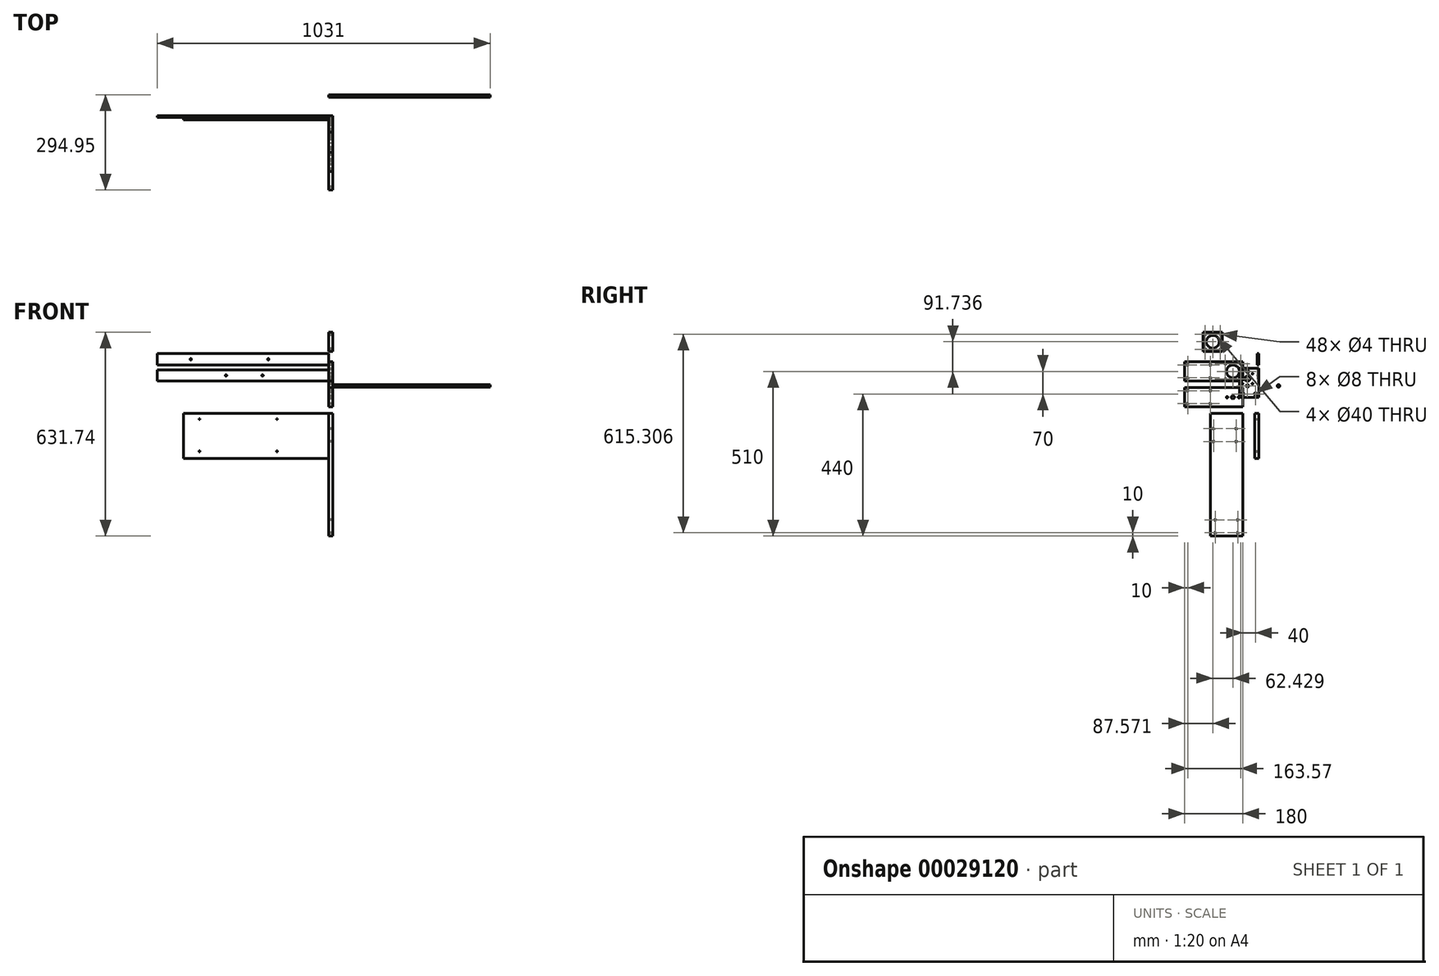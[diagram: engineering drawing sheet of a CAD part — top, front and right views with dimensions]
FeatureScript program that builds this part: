
annotation { "Feature Type Name" : "Feature", "Feature Type Description" : "" }
export const myFeature = defineFeature(function(context is Context, id is Id, definition is map)
    precondition{}
    {
        {
            var Q0;
            Q0=qCreatedBy(makeId("Right.planeOp"),FACE);
            var sketch = newSketch(context, id + "F0", { "sketchPlane" : qUnion([Q0])});
            skLineSegment(sketch, "E0.bottom", {"start": v(-60, 90) * mm, "end": v(0, 90) * mm});
            skLineSegment(sketch, "E0.top", {"start": v(-60, 0) * mm, "end": v(0, 0) * mm});
            skLineSegment(sketch, "E0.left", {"start": v(-60, 90) * mm, "end": v(-60, 0) * mm});
            skLineSegment(sketch, "E0.right", {"start": v(0, 90) * mm, "end": v(0, 0) * mm});
            skCircle(sketch, "E1", {"center": v(-50, 10) * mm, "radius": 4 * mm});
            skCircle(sketch, "E2", {"center": v(-10, 10) * mm, "radius": 4 * mm});
            skCircle(sketch, "E3", {"center": v(-35, 80) * mm, "radius": 4 * mm});
            skCircle(sketch, "E4", {"center": v(-35, 35) * mm, "radius": 4 * mm});
            skCircle(sketch, "E5", {"center": v(-19.5, 42) * mm, "radius": 1.5 * mm});
            skCircle(sketch, "E6.0.1.0", {"center": v(-19.5, 73) * mm, "radius": 1.5 * mm});
            skCircle(sketch, "E6.1.0.0", {"center": v(-50.5, 42) * mm, "radius": 1.5 * mm});
            skCircle(sketch, "E6.1.1.0", {"center": v(-50.5, 73) * mm, "radius": 1.5 * mm});
            skLineSegment(sketch, "E6.direction1", {"start": v(-19.5, 42) * mm, "end": v(-50.5, 42) * mm, "construction": true});
            skLineSegment(sketch, "E6.direction2", {"start": v(-19.5, 42) * mm, "end": v(-19.5, 73) * mm, "construction": true});
            skCircle(sketch, "E7", {"center": v(-35, 57.5) * mm, "radius": 8 * mm});
            skSolve(sketch);
        }
        {
            var Q0;
            Q0=makeQuery(id+"F0.imprint","IMPRINT",FACE,{"disambiguationData":[TD([[makeQuery(id+"F0.imprint","IMPRINT",EDGE,{"derivedFrom":sQuery(id+"F0.wireOp",EDGE,"E0.bottom")}),-1.0]])]});
            extrude(context, id + "F1", {"entities" : qUnion([Q0]), "depth" : 12.7 * mm});
        }
        {
            var Q0;
            Q0=makeQuery(id+"F1.opExtrude","SWEPT_FACE",FACE,{"disambiguationData":[OSD([sQuery(id+"F0.wireOp",EDGE,"E0.top")])]});
            var sketch = newSketch(context, id + "F2", { "sketchPlane" : qUnion([Q0])});
            skCircle(sketch, "E8", {"center": v(6.35, 50) * mm, "radius": 1.5 * mm});
            skCircle(sketch, "E9", {"center": v(6.35, 10) * mm, "radius": 1.5 * mm});
            skSolve(sketch);
        }
        {
            var Q0;
            Q0=makeQuery(id+"F2.imprint","IMPRINT",FACE,{"disambiguationData":[TD([[makeQuery(id+"F2.imprint","IMPRINT",EDGE,{"derivedFrom":sQuery(id+"F2.wireOp",EDGE,"E8")}),1.0]])]});
            var Q1;
            Q1=makeQuery(id+"F2.imprint","IMPRINT",FACE,{"disambiguationData":[TD([[makeQuery(id+"F2.imprint","IMPRINT",EDGE,{"derivedFrom":sQuery(id+"F2.wireOp",EDGE,"E9")}),1.0]])]});
            extrude(context, id + "F3", {"entities" : qUnion([Q0, Q1]), "operationType" : NewBodyOperationType.REMOVE, "endBound" : BoundingType.UP_TO_NEXT, "oppositeDirection" : true, "depth" : 25 * mm});
        }
        {
            var Q0;
            Q0=qCreatedBy(makeId("Front.planeOp"),FACE);
            var sketch = newSketch(context, id + "F4", { "sketchPlane" : qUnion([Q0])});
            skLineSegment(sketch, "E10.bottom", {"start": v(-531, 85) * mm, "end": v(0, 85) * mm});
            skLineSegment(sketch, "E10.top", {"start": v(-531, 50) * mm, "end": v(0, 50) * mm});
            skLineSegment(sketch, "E10.left", {"start": v(-531, 85) * mm, "end": v(-531, 50) * mm});
            skLineSegment(sketch, "E10.right", {"start": v(0, 85) * mm, "end": v(0, 50) * mm});
            skCircle(sketch, "E11", {"center": v(-317.8, 67.5) * mm, "radius": 2.37 * mm});
            skCircle(sketch, "E12", {"center": v(-204.65, 67.5) * mm, "radius": 2.38 * mm});
            skSolve(sketch);
        }
        {
            var Q0;
            Q0=makeQuery(id+"F4.imprint","IMPRINT",FACE,{"disambiguationData":[TD([[makeQuery(id+"F4.imprint","IMPRINT",EDGE,{"derivedFrom":sQuery(id+"F4.wireOp",EDGE,"E10.bottom")}),-1.0]])]});
            extrude(context, id + "F5", {"entities" : qUnion([Q0]), "depth" : 5 * mm});
        }
        {
            var Q0;
            Q0=qCreatedBy(makeId("Front.planeOp"),FACE);
            var sketch = newSketch(context, id + "F6", { "sketchPlane" : qUnion([Q0])});
            skLineSegment(sketch, "E13.bottom", {"start": v(-531, 135) * mm, "end": v(0, 135) * mm});
            skLineSegment(sketch, "E13.top", {"start": v(-531, 100) * mm, "end": v(0, 100) * mm});
            skLineSegment(sketch, "E13.left", {"start": v(-531, 135) * mm, "end": v(-531, 100) * mm});
            skLineSegment(sketch, "E13.right", {"start": v(0, 135) * mm, "end": v(0, 100) * mm});
            skCircle(sketch, "E14", {"center": v(-427, 117.5) * mm, "radius": 2.37 * mm});
            skCircle(sketch, "E15", {"center": v(-187, 117.5) * mm, "radius": 2.38 * mm});
            skSolve(sketch);
        }
        {
            var Q0;
            Q0=makeQuery(id+"F6.imprint","IMPRINT",FACE,{"disambiguationData":[TD([[makeQuery(id+"F6.imprint","IMPRINT",EDGE,{"derivedFrom":sQuery(id+"F6.wireOp",EDGE,"E13.bottom")}),-1.0]])]});
            extrude(context, id + "F7", {"entities" : qUnion([Q0]), "depth" : 5 * mm});
        }
        {
            var Q0;
            Q0=qCreatedBy(makeId("Front.planeOp"),FACE);
            var sketch = newSketch(context, id + "F8", { "sketchPlane" : qUnion([Q0])});
            skLineSegment(sketch, "E16.bottom", {"start": v(-450, -50) * mm, "end": v(0, -50) * mm});
            skLineSegment(sketch, "E16.top", {"start": v(-450, -190) * mm, "end": v(0, -190) * mm});
            skLineSegment(sketch, "E16.left", {"start": v(-450, -50) * mm, "end": v(-450, -190) * mm});
            skLineSegment(sketch, "E16.right", {"start": v(0, -50) * mm, "end": v(0, -190) * mm});
            skCircle(sketch, "E17", {"center": v(-400, -67.5) * mm, "radius": 1.5 * mm});
            skCircle(sketch, "E18", {"center": v(-160, -67.5) * mm, "radius": 1.5 * mm});
            skCircle(sketch, "E19", {"center": v(-400, -167.5) * mm, "radius": 1.5 * mm});
            skCircle(sketch, "E20", {"center": v(-160, -167.5) * mm, "radius": 1.5 * mm});
            skSolve(sketch);
        }
        {
            var Q0;
            Q0=makeQuery(id+"F8.imprint","IMPRINT",FACE,{"disambiguationData":[TD([[makeQuery(id+"F8.imprint","IMPRINT",EDGE,{"derivedFrom":sQuery(id+"F8.wireOp",EDGE,"E16.bottom")}),-1.0]])]});
            extrude(context, id + "F9", {"entities" : qUnion([Q0]), "depth" : 12.7 * mm});
        }
        {
            var Q0;
            Q0=qCreatedBy(makeId("Right.planeOp"),FACE);
            var sketch = newSketch(context, id + "F10", { "sketchPlane" : qUnion([Q0])});
            skLineSegment(sketch, "E21.bottom", {"start": v(-150, -50) * mm, "end": v(-50, -50) * mm});
            skLineSegment(sketch, "E21.top", {"start": v(-150, -430) * mm, "end": v(-50, -430) * mm});
            skLineSegment(sketch, "E21.left", {"start": v(-150, -50) * mm, "end": v(-150, -430) * mm});
            skLineSegment(sketch, "E21.right", {"start": v(-50, -50) * mm, "end": v(-50, -430) * mm});
            skLineSegment(sketch, "E22", {"start": v(-140, -97.5) * mm, "end": v(-70, -137.5) * mm, "construction": true});
            skPoint(sketch, "E23", {"position": v(-105, -117.5) * mm});
            skCircle(sketch, "E24", {"center": v(-70, -97.5) * mm, "radius": 2 * mm});
            skCircle(sketch, "E25", {"center": v(-140, -137.5) * mm, "radius": 2 * mm});
            skCircle(sketch, "E26", {"center": v(-140, -97.5) * mm, "radius": 2 * mm});
            skCircle(sketch, "E27", {"center": v(-70, -137.5) * mm, "radius": 2 * mm});
            skLineSegment(sketch, "E28", {"start": v(-50, -50) * mm, "end": v(-150, -430) * mm, "construction": true});
            skPoint(sketch, "E29", {"position": v(-100, -240) * mm});
            skLineSegment(sketch, "E30", {"start": v(-135, -380) * mm, "end": v(-65, -420) * mm, "construction": true});
            skPoint(sketch, "E31", {"position": v(-100, -400) * mm});
            skCircle(sketch, "E32", {"center": v(-65, -380) * mm, "radius": 2 * mm});
            skCircle(sketch, "E33", {"center": v(-135, -420) * mm, "radius": 2 * mm});
            skCircle(sketch, "E34", {"center": v(-135, -380) * mm, "radius": 2 * mm});
            skCircle(sketch, "E35", {"center": v(-65, -420) * mm, "radius": 2 * mm});
            skSolve(sketch);
        }
        {
            var Q0;
            Q0 = qSketchRegion(id + "F10", true);
            extrude(context, id + "F11", {"entities" : qUnion([Q0]), "depth" : 12.7 * mm});
        }
        {
            var Q0;
            Q0=qCreatedBy(makeId("Right.planeOp"),FACE);
            var sketch = newSketch(context, id + "F12", { "sketchPlane" : qUnion([Q0])});
            skLineSegment(sketch, "E36.bottom", {"start": v(-50, 110) * mm, "end": v(-230, 110) * mm});
            skLineSegment(sketch, "E36.top", {"start": v(-50, 50) * mm, "end": v(-230, 50) * mm});
            skLineSegment(sketch, "E36.left", {"start": v(-50, 110) * mm, "end": v(-50, 50) * mm});
            skLineSegment(sketch, "E36.right", {"start": v(-230, 110) * mm, "end": v(-230, 50) * mm});
            skCircle(sketch, "E37", {"center": v(-220, 100) * mm, "radius": 2 * mm});
            skCircle(sketch, "E38", {"center": v(-220, 60) * mm, "radius": 2 * mm});
            skCircle(sketch, "E39", {"center": v(-150, 100) * mm, "radius": 2 * mm});
            skCircle(sketch, "E40", {"center": v(-150, 60) * mm, "radius": 2 * mm});
            skLineSegment(sketch, "E41", {"start": v(-50, 110) * mm, "end": v(-230, 50) * mm, "construction": true});
            skLineSegment(sketch, "E42", {"start": v(-220, 100) * mm, "end": v(-150, 60) * mm, "construction": true});
            skPoint(sketch, "E43", {"position": v(-140, 80) * mm});
            skPoint(sketch, "E44", {"position": v(-185, 80) * mm});
            skLineSegment(sketch, "E45", {"start": v(-56.43, 56.43) * mm, "end": v(-103.57, 103.57) * mm, "construction": true});
            skLineSegment(sketch, "E46", {"start": v(-56.43, 103.57) * mm, "end": v(-103.57, 56.43) * mm, "construction": true});
            skPoint(sketch, "E47", {"position": v(-80, 80) * mm});
            skCircle(sketch, "E48", {"center": v(-80, 80) * mm, "radius": 20 * mm});
            skCircle(sketch, "E49", {"center": v(-56.43, 103.57) * mm, "radius": 2 * mm});
            skCircle(sketch, "E50.0.1.0", {"center": v(-56.43, 56.43) * mm, "radius": 2 * mm});
            skCircle(sketch, "E50.1.0.0", {"center": v(-103.57, 103.57) * mm, "radius": 2 * mm});
            skCircle(sketch, "E50.1.1.0", {"center": v(-103.57, 56.43) * mm, "radius": 2 * mm});
            skLineSegment(sketch, "E50.direction1", {"start": v(-56.43, 103.57) * mm, "end": v(-103.57, 103.57) * mm, "construction": true});
            skLineSegment(sketch, "E50.direction2", {"start": v(-56.43, 103.57) * mm, "end": v(-56.43, 56.43) * mm, "construction": true});
            skSolve(sketch);
        }
        {
            var Q0;
            Q0 = qSketchRegion(id + "F12", true);
            extrude(context, id + "F13", {"entities" : qUnion([Q0]), "depth" : 12.7 * mm});
        }
        {
            var Q0;
            Q0=qCreatedBy(makeId("Right.planeOp"),FACE);
            var sketch = newSketch(context, id + "F14", { "sketchPlane" : qUnion([Q0])});
            skLineSegment(sketch, "E51.bottom", {"start": v(-50, 30) * mm, "end": v(-230, 30) * mm});
            skLineSegment(sketch, "E51.top", {"start": v(-50, -30) * mm, "end": v(-230, -30) * mm});
            skLineSegment(sketch, "E51.left", {"start": v(-50, 30) * mm, "end": v(-50, -30) * mm});
            skLineSegment(sketch, "E51.right", {"start": v(-230, 30) * mm, "end": v(-230, -30) * mm});
            skCircle(sketch, "E52", {"center": v(-220, 20) * mm, "radius": 2 * mm});
            skCircle(sketch, "E53", {"center": v(-220, -20) * mm, "radius": 2 * mm});
            skCircle(sketch, "E54", {"center": v(-150, 20) * mm, "radius": 2 * mm});
            skCircle(sketch, "E55", {"center": v(-150, -20) * mm, "radius": 2 * mm});
            skLineSegment(sketch, "E56", {"start": v(-50, 30) * mm, "end": v(-230, -30) * mm, "construction": true});
            skLineSegment(sketch, "E57", {"start": v(-220, 20) * mm, "end": v(-150, -20) * mm, "construction": true});
            skPoint(sketch, "E58", {"position": v(-140, 0) * mm});
            skPoint(sketch, "E59", {"position": v(-185, 0) * mm});
            skPoint(sketch, "E60", {"position": v(-80, 0) * mm});
            skCircle(sketch, "E61", {"center": v(-80, 0) * mm, "radius": 5 * mm});
            skCircle(sketch, "E62", {"center": v(-61.75, 0) * mm, "radius": 2.5 * mm});
            skCircle(sketch, "E63", {"center": v(-98.25, 0) * mm, "radius": 2.5 * mm});
            skLineSegment(sketch, "E64", {"start": v(-61.75, 0) * mm, "end": v(-98.25, 0) * mm, "construction": true});
            skSolve(sketch);
        }
        {
            var Q0;
            Q0=makeQuery(id+"F14.imprint","IMPRINT",FACE,{"disambiguationData":[TD([[makeQuery(id+"F14.imprint","IMPRINT",EDGE,{"derivedFrom":sQuery(id+"F14.wireOp",EDGE,"E51.bottom")}),1.0]])]});
            extrude(context, id + "F15", {"entities" : qUnion([Q0]), "depth" : 12.7 * mm});
        }
        {
            var Q0;
            Q0=qCreatedBy(makeId("Right.planeOp"),FACE);
            var sketch = newSketch(context, id + "F16", { "sketchPlane" : qUnion([Q0])});
            skLineSegment(sketch, "E65.bottom", {"start": v(-112.43, 201.74) * mm, "end": v(-172.43, 201.74) * mm});
            skLineSegment(sketch, "E65.top", {"start": v(-112.43, 141.74) * mm, "end": v(-172.43, 141.74) * mm});
            skLineSegment(sketch, "E65.left", {"start": v(-112.43, 201.74) * mm, "end": v(-112.43, 141.74) * mm});
            skLineSegment(sketch, "E65.right", {"start": v(-172.43, 201.74) * mm, "end": v(-172.43, 141.74) * mm});
            skPoint(sketch, "E66", {"position": v(-142.43, 171.74) * mm});
            skCircle(sketch, "E67", {"center": v(-142.43, 171.74) * mm, "radius": 20 * mm});
            skLineSegment(sketch, "E68.direction2", {"start": v(-118.86, 195.3) * mm, "end": v(-118.86, 148.17) * mm, "construction": true});
            skLineSegment(sketch, "E69", {"start": v(-118.86, 195.3) * mm, "end": v(-166, 148.17) * mm, "construction": true});
            skLineSegment(sketch, "E70", {"start": v(-118.86, 148.17) * mm, "end": v(-166, 195.3) * mm, "construction": true});
            skCircle(sketch, "E68.1.0.0", {"center": v(-166, 195.3) * mm, "radius": 2 * mm});
            skCircle(sketch, "E68.0.1.0", {"center": v(-118.86, 148.17) * mm, "radius": 2 * mm});
            skCircle(sketch, "E71", {"center": v(-118.86, 195.3) * mm, "radius": 2 * mm});
            skLineSegment(sketch, "E68.direction1", {"start": v(-118.86, 195.3) * mm, "end": v(-166, 195.3) * mm, "construction": true});
            skCircle(sketch, "E68.1.1.0", {"center": v(-166, 148.17) * mm, "radius": 2 * mm});
            skLineSegment(sketch, "E72", {"start": v(-172.43, 201.74) * mm, "end": v(-112.43, 141.74) * mm, "construction": true});
            skSolve(sketch);
        }
        {
            var Q0;
            Q0=makeQuery(id+"F16.imprint","IMPRINT",FACE,{"disambiguationData":[TD([[makeQuery(id+"F16.imprint","IMPRINT",EDGE,{"derivedFrom":sQuery(id+"F16.wireOp",EDGE,"E65.bottom")}),1.0]])]});
            extrude(context, id + "F17", {"entities" : qUnion([Q0]), "depth" : 12.7 * mm});
        }
        {
            var Q0;
            Q0=qCreatedBy(makeId("Right.planeOp"),FACE);
            var sketch = newSketch(context, id + "F18", { "sketchPlane" : qUnion([Q0])});
            skCircle(sketch, "E73", {"center": v(60.95, 35.13) * mm, "radius": 4 * mm});
            skSolve(sketch);
        }
        {
            var Q0;
            Q0 = qSketchRegion(id + "F18", true);
            extrude(context, id + "F19", {"entities" : qUnion([Q0]), "depth" : 500 * mm});
        }
    });
